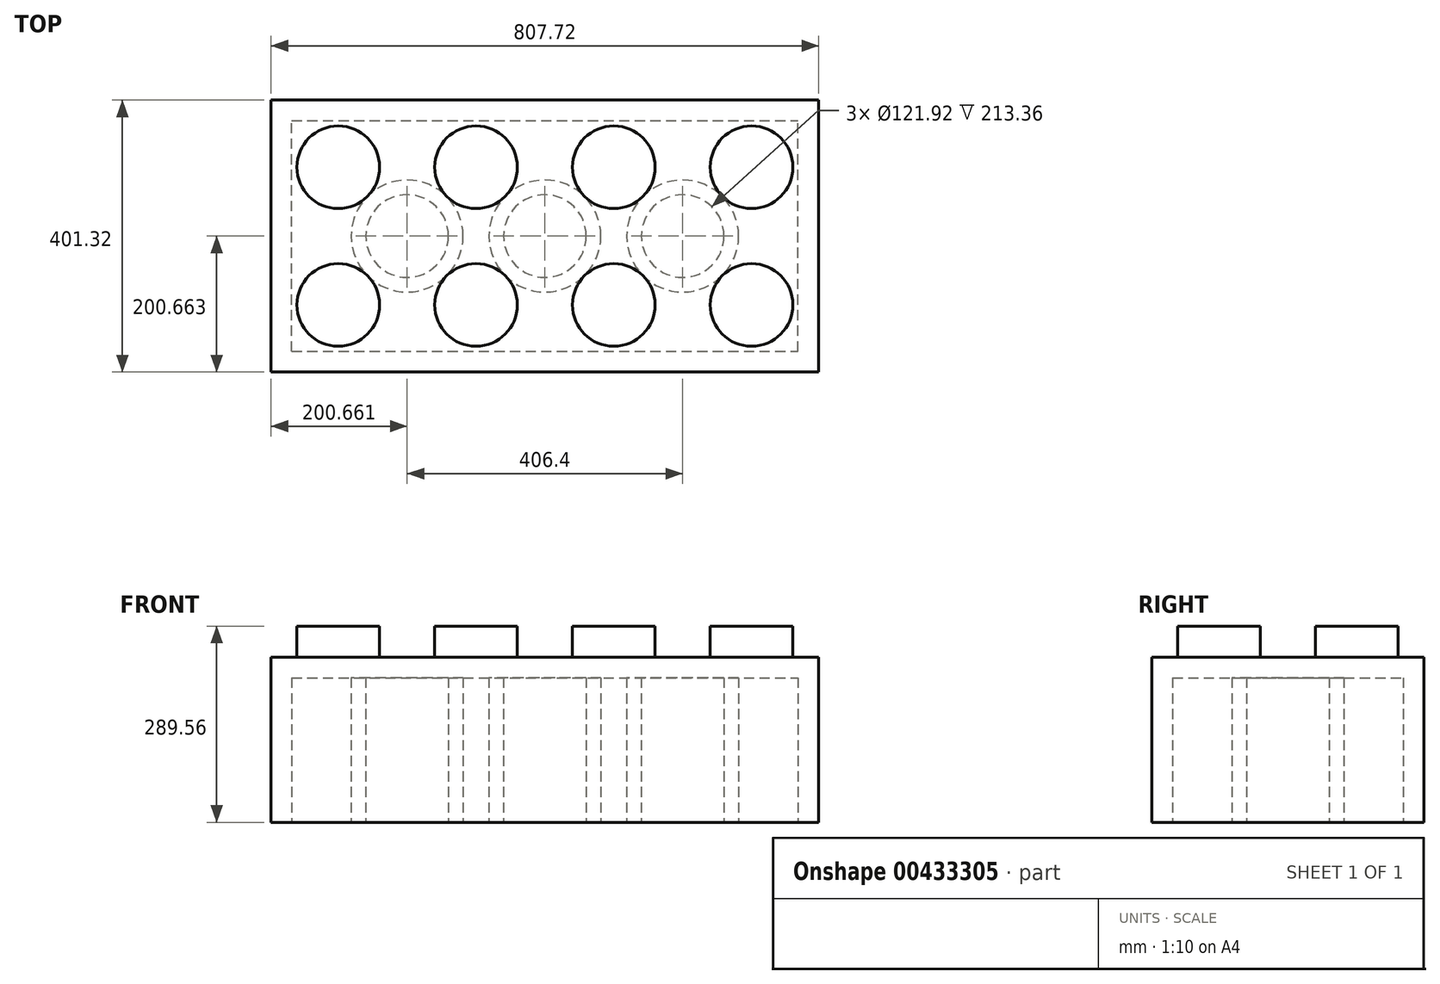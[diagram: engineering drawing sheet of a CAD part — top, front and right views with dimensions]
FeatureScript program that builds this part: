
annotation { "Feature Type Name" : "Feature", "Feature Type Description" : "" }
export const myFeature = defineFeature(function(context is Context, id is Id, definition is map)
    precondition{}
    {
        {
            var Q0;
            Q0=qCreatedBy(makeId("Top.planeOp"),FACE);
            var sketch = newSketch(context, id + "F0", { "sketchPlane" : qUnion([Q0])});
            skLineSegment(sketch, "E0.bottom", {"start": v(-467.62, 182.71) * mm, "end": v(340.1, 182.71) * mm});
            skLineSegment(sketch, "E0.top", {"start": v(-467.62, -218.6) * mm, "end": v(340.1, -218.6) * mm});
            skLineSegment(sketch, "E0.left", {"start": v(-467.62, 182.71) * mm, "end": v(-467.62, -218.6) * mm});
            skLineSegment(sketch, "E0.right", {"start": v(340.1, 182.71) * mm, "end": v(340.1, -218.6) * mm});
            skSolve(sketch);
        }
        {
            var Q0;
            Q0=makeQuery(id+"F0.imprint","IMPRINT",FACE,{"disambiguationData":[TD([[makeQuery(id+"F0.imprint","IMPRINT",EDGE,{"derivedFrom":sQuery(id+"F0.wireOp",EDGE,"E0.bottom")}),-1.0]])]});
            extrude(context, id + "F1", {"entities" : qUnion([Q0]), "depth" : 243.84 * mm});
        }
        {
            var Q0;
            Q0=makeQuery(id+"F1.opExtrude","CAP_FACE",FACE,{"disambiguationData":[OSD([sQuery(id+"F0.wireOp",EDGE,"E0.bottom"),sQuery(id+"F0.wireOp",EDGE,"E0.top"),sQuery(id+"F0.wireOp",EDGE,"E0.left"),sQuery(id+"F0.wireOp",EDGE,"E0.right")])],"isStart":false});
            var sketch = newSketch(context, id + "F2", { "sketchPlane" : qUnion([Q0])});
            skCircle(sketch, "E1", {"center": v(241.04, -119.55) * mm, "radius": 60.96 * mm});
            skCircle(sketch, "E2.0.1.0", {"center": v(241.04, 83.65) * mm, "radius": 60.96 * mm});
            skCircle(sketch, "E2.1.0.0", {"center": v(37.84, -119.55) * mm, "radius": 60.96 * mm});
            skCircle(sketch, "E2.1.1.0", {"center": v(37.84, 83.65) * mm, "radius": 60.96 * mm});
            skCircle(sketch, "E2.2.0.0", {"center": v(-165.36, -119.55) * mm, "radius": 60.96 * mm});
            skCircle(sketch, "E2.2.1.0", {"center": v(-165.36, 83.65) * mm, "radius": 60.96 * mm});
            skCircle(sketch, "E2.3.0.0", {"center": v(-368.56, -119.55) * mm, "radius": 60.96 * mm});
            skCircle(sketch, "E2.3.1.0", {"center": v(-368.56, 83.65) * mm, "radius": 60.96 * mm});
            skLineSegment(sketch, "E2.direction1", {"start": v(241.04, -119.55) * mm, "end": v(37.84, -119.55) * mm, "construction": true});
            skLineSegment(sketch, "E2.direction2", {"start": v(241.04, -119.55) * mm, "end": v(241.04, 83.65) * mm, "construction": true});
            skSolve(sketch);
        }
        {
            var Q0;
            Q0=makeQuery(id+"F2.imprint","IMPRINT",FACE,{"disambiguationData":[TD([[makeQuery(id+"F2.imprint","IMPRINT",EDGE,{"derivedFrom":sQuery(id+"F2.wireOp",EDGE,"E2.3.1.0")}),1.0]])]});
            var Q1;
            Q1=makeQuery(id+"F2.imprint","IMPRINT",FACE,{"disambiguationData":[TD([[makeQuery(id+"F2.imprint","IMPRINT",EDGE,{"derivedFrom":sQuery(id+"F2.wireOp",EDGE,"E2.2.1.0")}),1.0]])]});
            var Q2;
            Q2=makeQuery(id+"F2.imprint","IMPRINT",FACE,{"disambiguationData":[TD([[makeQuery(id+"F2.imprint","IMPRINT",EDGE,{"derivedFrom":sQuery(id+"F2.wireOp",EDGE,"E2.1.1.0")}),1.0]])]});
            var Q3;
            Q3=makeQuery(id+"F2.imprint","IMPRINT",FACE,{"disambiguationData":[TD([[makeQuery(id+"F2.imprint","IMPRINT",EDGE,{"derivedFrom":sQuery(id+"F2.wireOp",EDGE,"E2.0.1.0")}),1.0]])]});
            var Q4;
            Q4=makeQuery(id+"F2.imprint","IMPRINT",FACE,{"disambiguationData":[TD([[makeQuery(id+"F2.imprint","IMPRINT",EDGE,{"derivedFrom":sQuery(id+"F2.wireOp",EDGE,"E1")}),1.0]])]});
            var Q5;
            Q5=makeQuery(id+"F2.imprint","IMPRINT",FACE,{"disambiguationData":[TD([[makeQuery(id+"F2.imprint","IMPRINT",EDGE,{"derivedFrom":sQuery(id+"F2.wireOp",EDGE,"E2.1.0.0")}),1.0]])]});
            var Q6;
            Q6=makeQuery(id+"F2.imprint","IMPRINT",FACE,{"disambiguationData":[TD([[makeQuery(id+"F2.imprint","IMPRINT",EDGE,{"derivedFrom":sQuery(id+"F2.wireOp",EDGE,"E2.2.0.0")}),1.0]])]});
            var Q7;
            Q7=makeQuery(id+"F2.imprint","IMPRINT",FACE,{"disambiguationData":[TD([[makeQuery(id+"F2.imprint","IMPRINT",EDGE,{"derivedFrom":sQuery(id+"F2.wireOp",EDGE,"E2.3.0.0")}),1.0]])]});
            extrude(context, id + "F3", {"entities" : qUnion([Q0, Q1, Q2, Q3, Q4, Q5, Q6, Q7]), "operationType" : NewBodyOperationType.ADD, "depth" : 45.72 * mm});
        }
        {
            var Q0;
            Q0=makeQuery(id+"F0.imprint","IMPRINT",FACE,{"disambiguationData":[TD([[makeQuery(id+"F0.imprint","IMPRINT",EDGE,{"derivedFrom":sQuery(id+"F0.wireOp",EDGE,"E0.bottom")}),-1.0]])]});
            var sketch = newSketch(context, id + "F4", { "sketchPlane" : qUnion([Q0])});
            skCircle(sketch, "E3", {"center": v(-63.76, -17.95) * mm, "radius": 82.55 * mm});
            skCircle(sketch, "E4", {"center": v(-63.76, -17.95) * mm, "radius": 60.96 * mm});
            skCircle(sketch, "E5.1.0.0", {"center": v(139.44, -17.95) * mm, "radius": 82.55 * mm});
            skCircle(sketch, "E5.1.0.1", {"center": v(139.44, -17.95) * mm, "radius": 60.96 * mm});
            skLineSegment(sketch, "E5.direction1", {"start": v(-63.76, -17.95) * mm, "end": v(139.44, -17.95) * mm, "construction": true});
            skCircle(sketch, "E6.1.0.0", {"center": v(-266.96, -17.95) * mm, "radius": 60.96 * mm});
            skCircle(sketch, "E6.1.0.1", {"center": v(-266.96, -17.95) * mm, "radius": 82.55 * mm});
            skLineSegment(sketch, "E6.direction1", {"start": v(-63.76, -17.95) * mm, "end": v(-266.96, -17.95) * mm, "construction": true});
            skLineSegment(sketch, "E7.bottom", {"start": v(-437.14, -188.13) * mm, "end": v(309.62, -188.13) * mm});
            skLineSegment(sketch, "E7.top", {"start": v(-437.14, 152.23) * mm, "end": v(309.62, 152.23) * mm});
            skLineSegment(sketch, "E7.left", {"start": v(-437.14, -188.13) * mm, "end": v(-437.14, 152.23) * mm});
            skLineSegment(sketch, "E7.right", {"start": v(309.62, -188.13) * mm, "end": v(309.62, 152.23) * mm});
            skSolve(sketch);
        }
        {
            var Q0;
            Q0=makeQuery(id+"F4.imprint","IMPRINT",FACE,{"disambiguationData":[TD([[makeQuery(id+"F4.imprint","IMPRINT",EDGE,{"derivedFrom":sQuery(id+"F4.wireOp",EDGE,"E3")}),-1.0]])]});
            var Q1;
            Q1=makeQuery(id+"F4.imprint","IMPRINT",FACE,{"disambiguationData":[TD([[makeQuery(id+"F4.imprint","IMPRINT",EDGE,{"derivedFrom":sQuery(id+"F4.wireOp",EDGE,"E6.1.0.0")}),1.0]])]});
            var Q2;
            Q2=makeQuery(id+"F4.imprint","IMPRINT",FACE,{"disambiguationData":[TD([[makeQuery(id+"F4.imprint","IMPRINT",EDGE,{"derivedFrom":sQuery(id+"F4.wireOp",EDGE,"E4")}),1.0]])]});
            var Q3;
            Q3=makeQuery(id+"F4.imprint","IMPRINT",FACE,{"disambiguationData":[TD([[makeQuery(id+"F4.imprint","IMPRINT",EDGE,{"derivedFrom":sQuery(id+"F4.wireOp",EDGE,"E5.1.0.1")}),1.0]])]});
            extrude(context, id + "F5", {"entities" : qUnion([Q0, Q1, Q2, Q3]), "operationType" : NewBodyOperationType.REMOVE, "depth" : 213.36 * mm});
        }
    });
